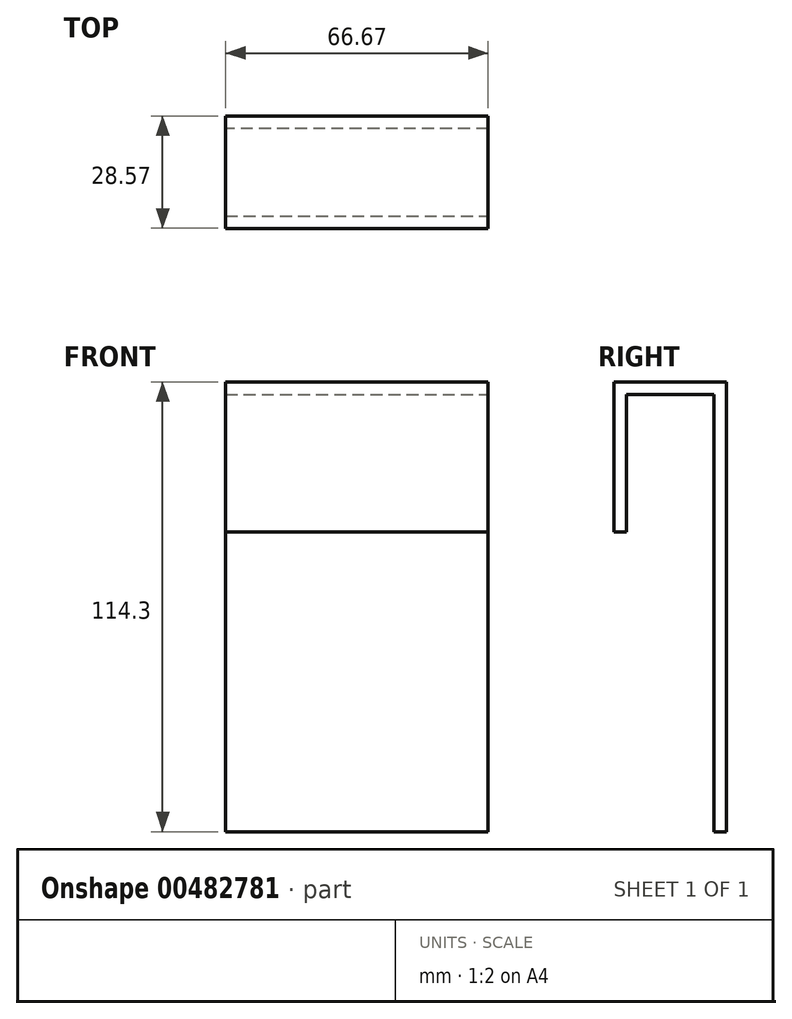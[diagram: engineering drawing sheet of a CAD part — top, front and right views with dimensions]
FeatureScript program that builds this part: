
annotation { "Feature Type Name" : "Feature", "Feature Type Description" : "" }
export const myFeature = defineFeature(function(context is Context, id is Id, definition is map)
    precondition{}
    {
        {
            var Q0;
            Q0=qCreatedBy(makeId("Front.planeOp"),FACE);
            var sketch = newSketch(context, id + "F0", { "sketchPlane" : qUnion([Q0])});
            skLineSegment(sketch, "E0.bottom", {"start": v(-31.75, 19.05) * mm, "end": v(31.75, 19.05) * mm});
            skLineSegment(sketch, "E0.top", {"start": v(-31.75, -19.05) * mm, "end": v(31.75, -19.05) * mm});
            skLineSegment(sketch, "E0.left", {"start": v(-31.75, 19.05) * mm, "end": v(-31.75, -19.05) * mm});
            skLineSegment(sketch, "E0.right", {"start": v(31.75, 19.05) * mm, "end": v(31.75, -19.05) * mm});
            skPoint(sketch, "E1", {"position": v(0, 0) * mm});
            skPoint(sketch, "E1.positionSnap0", {"position": v(-31.75, 0) * mm});
            skPoint(sketch, "E1.positionSnap1", {"position": v(0, 19.05) * mm});
            skSolve(sketch);
        }
        {
            var Q0;
            Q0=makeQuery(id+"F0.imprint","IMPRINT",FACE,{"disambiguationData":[TD([[makeQuery(id+"F0.imprint","IMPRINT",EDGE,{"derivedFrom":sQuery(id+"F0.wireOp",EDGE,"E0.bottom")}),-1.0]])]});
            extrude(context, id + "F1", {"entities" : qUnion([Q0]), "depth" : 3.17 * mm, "offsetDistance" : 25.4 * mm});
        }
        {
            var Q0;
            Q0=makeQuery(id+"F1.opExtrude","SWEPT_FACE",FACE,{"disambiguationData":[OSD([sQuery(id+"F0.wireOp",EDGE,"E0.right")])]});
            var sketch = newSketch(context, id + "F2", { "sketchPlane" : qUnion([Q0])});
            skLineSegment(sketch, "E2.bottom", {"start": v(-3.18, 19.05) * mm, "end": v(22.23, 19.05) * mm});
            skLineSegment(sketch, "E2.top", {"start": v(-3.18, -19.05) * mm, "end": v(22.23, -19.05) * mm});
            skLineSegment(sketch, "E2.left", {"start": v(-3.18, 19.05) * mm, "end": v(-3.18, -19.05) * mm});
            skLineSegment(sketch, "E2.right", {"start": v(22.23, 19.05) * mm, "end": v(22.23, -19.05) * mm});
            skSolve(sketch);
        }
        {
            var Q0;
            {var subQ2=sQuery(id+"F2.wireOp",EDGE,"E2.right");Q0=makeQuery(id+"F2.imprint","IMPRINT",FACE,{"disambiguationData":[TD([[makeQuery(id+"F2.imprint","IMPRINT",EDGE,{"derivedFrom":subQ2}),-1.0]])]});}
            var Q1;
            {var subQ2=sQuery(id+"F2.wireOp",EDGE,"E2.left");Q1=makeQuery(id+"F2.imprint","IMPRINT",FACE,{"disambiguationData":[TD([[makeQuery(id+"F2.imprint","IMPRINT",EDGE,{"derivedFrom":subQ2}),1.0]])]});}
            extrude(context, id + "F3", {"entities" : qUnion([Q0, Q1]), "operationType" : NewBodyOperationType.ADD, "depth" : 3.17 * mm, "offsetDistance" : 25.4 * mm});
        }
        {
            var Q0;
            Q0=makeQuery(id+"F3.boolean.opBoolean","MERGE",FACE,{"derivedFrom":[makeQuery(id+"F1.opExtrude","SWEPT_FACE",FACE,{"disambiguationData":[OSD([sQuery(id+"F0.wireOp",EDGE,"E0.top")])]}),makeQuery(id+"F3.opExtrude","SWEPT_FACE",FACE,{"disambiguationData":[OSD([sQuery(id+"F2.wireOp",EDGE,"E2.top")])]})]});
            var sketch = newSketch(context, id + "F4", { "sketchPlane" : qUnion([Q0])});
            skLineSegment(sketch, "E3.bottom", {"start": v(34.92, -22.23) * mm, "end": v(31.75, -22.23) * mm});
            skLineSegment(sketch, "E3.top", {"start": v(34.92, 3.18) * mm, "end": v(31.75, 3.18) * mm});
            skLineSegment(sketch, "E3.left", {"start": v(34.92, -22.23) * mm, "end": v(34.92, 3.18) * mm});
            skLineSegment(sketch, "E3.right", {"start": v(31.75, -22.23) * mm, "end": v(31.75, 3.18) * mm});
            skSolve(sketch);
        }
        {
            var Q0;
            {var subQ1=sQuery(id+"F4.wireOp",EDGE,"E3.bottom");Q0=makeQuery(id+"F4.imprint","IMPRINT",FACE,{"disambiguationData":[TD([[makeQuery(id+"F4.imprint","IMPRINT",EDGE,{"derivedFrom":subQ1}),-1.0]])]});}
            extrude(context, id + "F5", {"entities" : qUnion([Q0]), "operationType" : NewBodyOperationType.ADD, "depth" : 76.2 * mm});
        }
        {
            var Q0;
            Q0=makeQuery(id+"F5.boolean.opBoolean","MERGE",FACE,{"derivedFrom":[makeQuery(id+"F3.opExtrude","SWEPT_FACE",FACE,{"disambiguationData":[OSD([sQuery(id+"F2.wireOp",EDGE,"E2.right")])]}),makeQuery(id+"F5.opExtrude","SWEPT_FACE",FACE,{"disambiguationData":[OSD([sQuery(id+"F4.wireOp",EDGE,"E3.bottom")])]})]});
            var sketch = newSketch(context, id + "F6", { "sketchPlane" : qUnion([Q0])});
            skLineSegment(sketch, "E4.bottom", {"start": v(-31.75, 19.05) * mm, "end": v(31.75, 19.05) * mm});
            skLineSegment(sketch, "E4.top", {"start": v(-31.75, -95.25) * mm, "end": v(31.75, -95.25) * mm});
            skLineSegment(sketch, "E4.left", {"start": v(-31.75, 19.05) * mm, "end": v(-31.75, -95.25) * mm});
            skLineSegment(sketch, "E4.right", {"start": v(31.75, 19.05) * mm, "end": v(31.75, -95.25) * mm});
            skLineSegment(sketch, "E5.bottom", {"start": v(-34.92, 19.05) * mm, "end": v(-31.75, 19.05) * mm});
            skLineSegment(sketch, "E5.top", {"start": v(-34.92, -95.25) * mm, "end": v(-31.75, -95.25) * mm});
            skLineSegment(sketch, "E5.left", {"start": v(-34.92, 19.05) * mm, "end": v(-34.92, -95.25) * mm});
            skSolve(sketch);
        }
        {
            var Q0;
            Q0=makeQuery(id+"F6.imprint","IMPRINT",FACE,{"disambiguationData":[TD([[makeQuery(id+"F6.imprint","IMPRINT",EDGE,{"derivedFrom":sQuery(id+"F6.wireOp",EDGE,"E4.bottom")}),-1.0]])]});
            var Q1;
            Q1=makeQuery(id+"F6.imprint","IMPRINT",FACE,{"disambiguationData":[TD([[makeQuery(id+"F6.imprint","IMPRINT",EDGE,{"derivedFrom":sQuery(id+"F6.wireOp",EDGE,"E5.bottom")}),-1.0]])]});
            extrude(context, id + "F7", {"entities" : qUnion([Q0, Q1]), "operationType" : NewBodyOperationType.ADD, "depth" : 3.17 * mm, "offsetDistance" : 25.4 * mm});
        }
        {
            var Q0;
            Q0=makeQuery(id+"F7.boolean.opBoolean","MERGE",FACE,{"derivedFrom":[makeQuery(id+"F3.boolean.opBoolean","MERGE",FACE,{"derivedFrom":[makeQuery(id+"F1.opExtrude","SWEPT_FACE",FACE,{"disambiguationData":[OSD([sQuery(id+"F0.wireOp",EDGE,"E0.bottom")])]}),makeQuery(id+"F3.opExtrude","SWEPT_FACE",FACE,{"disambiguationData":[OSD([sQuery(id+"F2.wireOp",EDGE,"E2.bottom")])]})]}),makeQuery(id+"F7.opExtrude","SWEPT_FACE",FACE,{"disambiguationData":[OSD([sQuery(id+"F6.wireOp",EDGE,"E4.bottom"),sQuery(id+"F6.wireOp",EDGE,"E5.bottom")])]})]});
            var sketch = newSketch(context, id + "F8", { "sketchPlane" : qUnion([Q0])});
            skLineSegment(sketch, "E6.bottom", {"start": v(-31.75, 25.4) * mm, "end": v(34.92, 25.4) * mm});
            skLineSegment(sketch, "E6.top", {"start": v(-31.75, -3.18) * mm, "end": v(34.92, -3.18) * mm});
            skLineSegment(sketch, "E6.left", {"start": v(-31.75, 25.4) * mm, "end": v(-31.75, -3.18) * mm});
            skLineSegment(sketch, "E6.right", {"start": v(34.92, 25.4) * mm, "end": v(34.92, -3.18) * mm});
            skLineSegment(sketch, "E7.bottom", {"start": v(-31.75, 22.23) * mm, "end": v(31.75, 22.23) * mm});
            skLineSegment(sketch, "E7.top", {"start": v(-31.75, 0) * mm, "end": v(31.75, 0) * mm});
            skLineSegment(sketch, "E7.left", {"start": v(-31.75, 22.23) * mm, "end": v(-31.75, 0) * mm});
            skLineSegment(sketch, "E7.right", {"start": v(31.75, 22.23) * mm, "end": v(31.75, 0) * mm});
            skSolve(sketch);
        }
        {
            var Q0;
            Q0=makeQuery(id+"F8.imprint","IMPRINT",FACE,{"disambiguationData":[TD([[makeQuery(id+"F8.imprint","IMPRINT",EDGE,{"derivedFrom":sQuery(id+"F8.wireOp",EDGE,"E7.bottom")}),1.0]])]});
            extrude(context, id + "F9", {"entities" : qUnion([Q0]), "operationType" : NewBodyOperationType.ADD, "oppositeDirection" : true, "depth" : 3.17 * mm, "offsetDistance" : 25.4 * mm});
        }
        {
            var Q0;
            Q0=makeQuery(id+"F7.boolean.opBoolean","MERGE",FACE,{"derivedFrom":[makeQuery(id+"F5.opExtrude","CAP_FACE",FACE,{"disambiguationData":[OSD([sQuery(id+"F4.wireOp",EDGE,"E3.bottom"),sQuery(id+"F4.wireOp",EDGE,"E3.top"),sQuery(id+"F4.wireOp",EDGE,"E3.left"),sQuery(id+"F4.wireOp",EDGE,"E3.right")])],"isStart":false}),makeQuery(id+"F7.opExtrude","SWEPT_FACE",FACE,{"disambiguationData":[OSD([sQuery(id+"F6.wireOp",EDGE,"E4.top"),sQuery(id+"F6.wireOp",EDGE,"E5.top")])]})]});
            var sketch = newSketch(context, id + "F10", { "sketchPlane" : qUnion([Q0])});
            skLineSegment(sketch, "E8.bottom", {"start": v(31.75, 3.18) * mm, "end": v(34.92, 3.18) * mm});
            skLineSegment(sketch, "E8.top", {"start": v(31.75, -25.4) * mm, "end": v(34.92, -25.4) * mm});
            skLineSegment(sketch, "E8.left", {"start": v(31.75, 3.18) * mm, "end": v(31.75, -25.4) * mm});
            skLineSegment(sketch, "E8.right", {"start": v(34.92, 3.18) * mm, "end": v(34.92, -25.4) * mm});
            skSolve(sketch);
        }
        {
            var Q0;
            {var subQ5=sQuery(id+"F10.wireOp",EDGE,"E8.bottom");Q0=makeQuery(id+"F10.imprint","IMPRINT",FACE,{"disambiguationData":[TD([[makeQuery(id+"F10.imprint","IMPRINT",EDGE,{"derivedFrom":subQ5}),-1.0]])]});}
            extrude(context, id + "F11", {"entities" : qUnion([Q0]), "operationType" : NewBodyOperationType.REMOVE, "oppositeDirection" : true, "depth" : 76.2 * mm, "offsetDistance" : 25.4 * mm});
        }
        {
            var Q0;
            Q0=makeQuery(id+"F9.boolean.opBoolean","MERGE",FACE,{"derivedFrom":[makeQuery(id+"F1.opExtrude","SWEPT_FACE",FACE,{"disambiguationData":[OSD([sQuery(id+"F0.wireOp",EDGE,"E0.left")])]}),makeQuery(id+"F7.opExtrude","SWEPT_FACE",FACE,{"disambiguationData":[OSD([sQuery(id+"F6.wireOp",EDGE,"E4.right")])]}),makeQuery(id+"F9.opExtrude","SWEPT_FACE",FACE,{"disambiguationData":[OSD([sQuery(id+"F8.wireOp",EDGE,"E7.left")])]})]});
            var sketch = newSketch(context, id + "F12", { "sketchPlane" : qUnion([Q0])});
            skLineSegment(sketch, "E9.bottom", {"start": v(-25.4, 19.05) * mm, "end": v(3.18, 19.05) * mm});
            skLineSegment(sketch, "E9.top", {"start": v(-25.4, -95.25) * mm, "end": v(3.18, -95.25) * mm});
            skLineSegment(sketch, "E9.left", {"start": v(-25.4, 19.05) * mm, "end": v(-25.4, -95.25) * mm});
            skLineSegment(sketch, "E9.right", {"start": v(3.18, 19.05) * mm, "end": v(3.18, -95.25) * mm});
            skSolve(sketch);
        }
        {
            var Q0;
            Q0=makeQuery(id+"F12.imprint","IMPRINT",FACE,{"disambiguationData":[TD([[makeQuery(id+"F12.imprint","IMPRINT",EDGE,{"derivedFrom":makeQuery(id+"F9.opExtrude","CAP_EDGE",EDGE,{"disambiguationData":[OSD([sQuery(id+"F8.wireOp",EDGE,"E7.left")])],"isStart":false})}),-1.0]])]});
            var Q1;
            {var subQ4=sQuery(id+"F12.wireOp",EDGE,"E9.bottom");Q1=makeQuery(id+"F12.imprint","IMPRINT",FACE,{"disambiguationData":[TD([[makeQuery(id+"F12.imprint","IMPRINT",EDGE,{"derivedFrom":subQ4}),1.0]])]});}
            extrude(context, id + "F13", {"entities" : qUnion([Q0, Q1]), "operationType" : NewBodyOperationType.ADD, "depth" : 3.17 * mm, "offsetDistance" : 25.4 * mm});
        }
        {
            var Q0;
            Q0=makeQuery(id+"F7.boolean.opBoolean","MERGE",FACE,{"derivedFrom":[makeQuery(id+"F5.boolean.opBoolean","MERGE",FACE,{"derivedFrom":[makeQuery(id+"F3.opExtrude","CAP_FACE",FACE,{"disambiguationData":[OSD([sQuery(id+"F2.wireOp",EDGE,"E2.bottom"),sQuery(id+"F2.wireOp",EDGE,"E2.top"),sQuery(id+"F2.wireOp",EDGE,"E2.left"),sQuery(id+"F2.wireOp",EDGE,"E2.right")])],"isStart":false}),makeQuery(id+"F5.opExtrude","SWEPT_FACE",FACE,{"disambiguationData":[OSD([sQuery(id+"F4.wireOp",EDGE,"E3.left")])]})]}),makeQuery(id+"F7.opExtrude","SWEPT_FACE",FACE,{"disambiguationData":[OSD([sQuery(id+"F6.wireOp",EDGE,"E5.left")])]})]});
            var sketch = newSketch(context, id + "F14", { "sketchPlane" : qUnion([Q0])});
            skLineSegment(sketch, "E10.bottom", {"start": v(25.4, -19.05) * mm, "end": v(-3.18, -19.05) * mm});
            skLineSegment(sketch, "E10.top", {"start": v(25.4, 19.05) * mm, "end": v(-3.18, 19.05) * mm});
            skLineSegment(sketch, "E10.left", {"start": v(25.4, -19.05) * mm, "end": v(25.4, 19.05) * mm});
            skLineSegment(sketch, "E10.right", {"start": v(-3.18, -19.05) * mm, "end": v(-3.18, 19.05) * mm});
            skSolve(sketch);
        }
        {
            var Q0;
            Q0=makeQuery(id+"F14.imprint","IMPRINT",FACE,{"disambiguationData":[TD([[makeQuery(id+"F14.imprint","IMPRINT",EDGE,{"derivedFrom":sQuery(id+"F14.wireOp",EDGE,"E10.bottom")}),1.0]])]});
            extrude(context, id + "F15", {"entities" : qUnion([Q0]), "operationType" : NewBodyOperationType.REMOVE, "oppositeDirection" : true, "depth" : 3.17 * mm, "offsetDistance" : 25.4 * mm});
        }
    });
